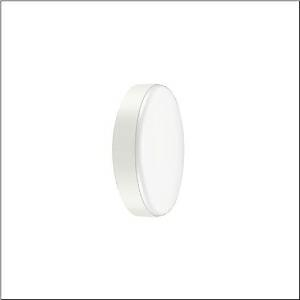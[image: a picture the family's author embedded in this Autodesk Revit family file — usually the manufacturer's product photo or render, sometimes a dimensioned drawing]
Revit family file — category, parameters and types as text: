
# Revit family: rondel_31_51wc10da32a
name_source: partatom
category: Lighting Fixtures
units: mm (PartAtom-declared; Revit-internal decimal feet)

## family parameters
Cut with Voids When Loaded = No
Host = Face
Light Source = No
Part Type = Normal
Room Calculation Point = No
Round Connector Dimension = Use Diameter
Shared = No

## types (1)
- Rondel 31 (1 x LED, 2450 lm, 19 W, 3000K)
    Apparent Load = 19 VA
    CIE Flux Codes = 44 75 94 94 100
    Color Rendering = 80
    Color Temperature = 3000K
    Default Elevation = 1800 mm
    Description = Rondel 31, wall and ceiling luminaire, primary optical cover: cover, of PC, opal, light emission: direct distribution, primary light characteristic: symmetric, installation type: surface-mounted, LED, rated luminous flux: 2.300lm, luminous efficacy: 120lm/W, light colour: 830, colour temperature: 3000K, with terminal, 5-pole, max. 2.5mm², mains connection: 220..240V, AC, 50/60Hz, rated input power: 19W, luminaire housing, of PC, traffic white (RAL 9016), diameter: 350mm, protection rating (complete): IP65, insulation class (complete): insulation class II (safety insulation), certification: CE, impact resistance: IK10, permissible storage temperature: -20..+60°C, packaging unit: 1 piece
    Height = 97 mm
    Lamp = 1 x LED
    Lamp Light Flux = 2450 lm
    Lamp Power = 19 W
    Lamp count = 1
    Length = 350 mm
    Luminous efficacy = 129 lm/W
    Manufacturer = Siteco
    ModVariant = No
    Model = 51WC10DA32A
    Mounting Place = Ceiling
    Mounting Type = Surface mounted
    Number of Poles = 1
    OnlyDefault = Yes
    Power Factor = 1
    Product Name = Rondel 31
    Product group = wall and ceiling luminaire
    ProductGroupID = 301
    Protection Class = Protection class II
    Protection Degree = IP 65
    RLX_Detail_Level = 1
    RlxData = <blob elided: 29701 chars, md5=b96a0f21>
    Socket = socket
    Standby Power = 0 W
    System Light Flux = 2450 lm
    System Power = 19 W
    Type Comments = Product without accessories
    Type Image = l_1007027.jpg
    URL = http://relux.com
    VarID = ---
    Voltage = 0 V
    Weight = 0.00 kg
    Width = 0 mm  [stored 0 ft]

note: [stored X ft] marks values corroborated as IEEE doubles in the binary element streams (Revit-internal decimal feet)

## geometry (parser evidence)
native form markers: Blend x4, Sweep x9
no freeform markers — native parametric forms only
